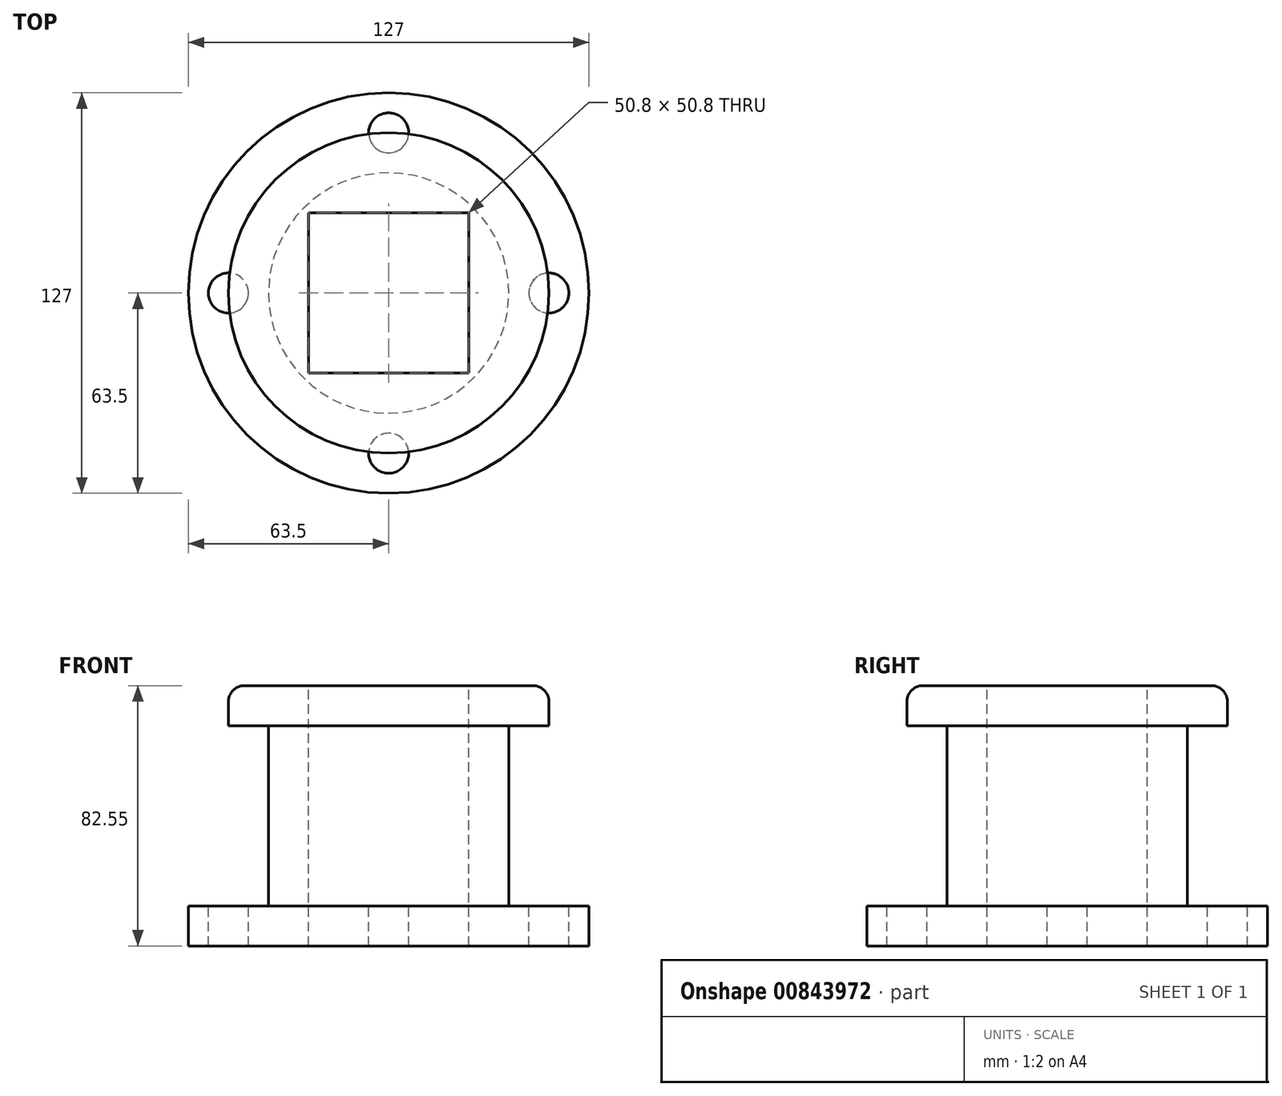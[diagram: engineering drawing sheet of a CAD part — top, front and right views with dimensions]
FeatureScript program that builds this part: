
annotation { "Feature Type Name" : "Feature", "Feature Type Description" : "" }
export const myFeature = defineFeature(function(context is Context, id is Id, definition is map)
    precondition{}
    {
        {
            var Q0;
            Q0=qCreatedBy(makeId("Top.planeOp"),FACE);
            var sketch = newSketch(context, id + "F0", { "sketchPlane" : qUnion([Q0])});
            skCircle(sketch, "E0", {"center": v(0, 0) * mm, "radius": 63.5 * mm});
            skSolve(sketch);
        }
        {
            var Q0;
            Q0 = qSketchRegion(id + "F0", true);
            extrude(context, id + "F1", {"entities" : qUnion([Q0]), "depth" : 12.7 * mm, "offsetDistance" : 25.4 * mm});
        }
        {
            var Q0;
            Q0=makeQuery(id+"F1.opExtrude","CAP_FACE",FACE,{"disambiguationData":[OSD([sQuery(id+"F0.wireOp",EDGE,"E0")])],"isStart":false});
            var sketch = newSketch(context, id + "F2", { "sketchPlane" : qUnion([Q0])});
            skCircle(sketch, "E1", {"center": v(0, 0) * mm, "radius": 38.1 * mm});
            skCircle(sketch, "E2", {"center": v(0, 50.8) * mm, "radius": 6.35 * mm});
            skCircle(sketch, "E3", {"center": v(-50.8, 0) * mm, "radius": 6.35 * mm});
            skCircle(sketch, "E4", {"center": v(50.8, 0) * mm, "radius": 6.35 * mm});
            skCircle(sketch, "E5", {"center": v(0, -50.8) * mm, "radius": 6.35 * mm});
            skSolve(sketch);
        }
        {
            var Q0;
            Q0=makeQuery(id+"F2.imprint","IMPRINT",FACE,{"disambiguationData":[TD([[makeQuery(id+"F2.imprint","IMPRINT",EDGE,{"derivedFrom":sQuery(id+"F2.wireOp",EDGE,"E2")}),1.0]])]});
            var Q1;
            Q1=makeQuery(id+"F2.imprint","IMPRINT",FACE,{"disambiguationData":[TD([[makeQuery(id+"F2.imprint","IMPRINT",EDGE,{"derivedFrom":sQuery(id+"F2.wireOp",EDGE,"E4")}),1.0]])]});
            var Q2;
            Q2=makeQuery(id+"F2.imprint","IMPRINT",FACE,{"disambiguationData":[TD([[makeQuery(id+"F2.imprint","IMPRINT",EDGE,{"derivedFrom":sQuery(id+"F2.wireOp",EDGE,"E5")}),1.0]])]});
            var Q3;
            Q3=makeQuery(id+"F2.imprint","IMPRINT",FACE,{"disambiguationData":[TD([[makeQuery(id+"F2.imprint","IMPRINT",EDGE,{"derivedFrom":sQuery(id+"F2.wireOp",EDGE,"E3")}),1.0]])]});
            extrude(context, id + "F3", {"entities" : qUnion([Q0, Q1, Q2, Q3]), "operationType" : NewBodyOperationType.REMOVE, "oppositeDirection" : true, "depth" : 12.7 * mm, "offsetDistance" : 25.4 * mm});
        }
        {
            var Q0;
            Q0=makeQuery(id+"F2.imprint","IMPRINT",FACE,{"disambiguationData":[TD([[makeQuery(id+"F2.imprint","IMPRINT",EDGE,{"derivedFrom":sQuery(id+"F2.wireOp",EDGE,"E1")}),1.0]])]});
            extrude(context, id + "F4", {"entities" : qUnion([Q0]), "operationType" : NewBodyOperationType.ADD, "depth" : 57.15 * mm, "offsetDistance" : 25.4 * mm});
        }
        {
            var Q0;
            Q0=makeQuery(id+"F4.opExtrude","CAP_FACE",FACE,{"disambiguationData":[OSD([sQuery(id+"F2.wireOp",EDGE,"E1")])],"isStart":false});
            var sketch = newSketch(context, id + "F5", { "sketchPlane" : qUnion([Q0])});
            skCircle(sketch, "E6", {"center": v(0, 0) * mm, "radius": 50.8 * mm});
            skSolve(sketch);
        }
        {
            var Q0;
            Q0 = qSketchRegion(id + "F5", true);
            extrude(context, id + "F6", {"entities" : qUnion([Q0]), "operationType" : NewBodyOperationType.ADD, "depth" : 12.7 * mm, "offsetDistance" : 25.4 * mm});
        }
        {
            var Q0;
            Q0=makeQuery(id+"F6.opExtrude","CAP_EDGE",EDGE,{"disambiguationData":[OSD([sQuery(id+"F5.wireOp",EDGE,"E6")])],"isStart":false});
            fillet(context, id + "F7", {"entities" : qUnion([Q0]), "radius" : 5.08 * mm, "tangentPropagation" : true, "allowEdgeOverflow" : false});
        }
        {
            var Q0;
            Q0=makeQuery(id+"F6.opExtrude","CAP_FACE",FACE,{"disambiguationData":[OSD([sQuery(id+"F5.wireOp",EDGE,"E6")])],"isStart":false});
            var sketch = newSketch(context, id + "F8", { "sketchPlane" : qUnion([Q0])});
            skLineSegment(sketch, "E7.bottom", {"start": v(25.4, -25.4) * mm, "end": v(-25.4, -25.4) * mm});
            skLineSegment(sketch, "E7.top", {"start": v(25.4, 25.4) * mm, "end": v(-25.4, 25.4) * mm});
            skLineSegment(sketch, "E7.left", {"start": v(25.4, -25.4) * mm, "end": v(25.4, 25.4) * mm});
            skLineSegment(sketch, "E7.right", {"start": v(-25.4, -25.4) * mm, "end": v(-25.4, 25.4) * mm});
            skPoint(sketch, "E7.middle", {"position": v(0, 0) * mm});
            skSolve(sketch);
        }
        {
            var Q0;
            Q0=makeQuery(id+"F8.imprint","IMPRINT",FACE,{"disambiguationData":[TD([[makeQuery(id+"F8.imprint","IMPRINT",EDGE,{"derivedFrom":sQuery(id+"F8.wireOp",EDGE,"E7.bottom")}),-1.0]])]});
            extrude(context, id + "F9", {"entities" : qUnion([Q0]), "operationType" : NewBodyOperationType.REMOVE, "oppositeDirection" : true, "depth" : 85.1 * mm, "offsetDistance" : 25.4 * mm});
        }
    });
